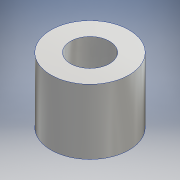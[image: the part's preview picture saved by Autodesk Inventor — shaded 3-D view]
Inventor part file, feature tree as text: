
AUTODESK INVENTOR PART (.ipt)
format: ipt  version: 2016 (Build 200138000, 138)  size: 96,256 bytes
history: native  units: mm
features: other x1, extrude x1, sketch x1
ambient origin geometry x8: Origin, YZ Plane, XZ Plane, XY Plane, X Axis, Y Axis, Z Axis, Center Point
bodies: Body1 (feature_tree)
feature tree (3):
  other  "ソリッド1"
  extrude  "押し出し1"  Depth=6.0mm
  sketch  "スケッチ1"
